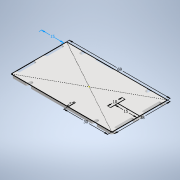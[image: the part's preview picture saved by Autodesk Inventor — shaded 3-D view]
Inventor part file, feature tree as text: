
AUTODESK INVENTOR PART (.ipt)
format: ipt  version: 2022 (Build 260153000, 153)  size: 303,616 bytes
history: native  units: mm
features: other x5, fillet x4, sketch x4, extrude x3, reference x3, projected_geometry x2, mirror x1
ambient origin geometry x8: Origin, YZ Plane, XZ Plane, XY Plane, X Axis, Y Axis, Z Axis, Center Point
bodies: Body1 (feature_tree)
feature tree (22):
  other  "Твердое тело1"
  extrude  "Выдавливание1"  Depth=69.0mm
  fillet  "Сопряжение1"  Radius=38.0mm
  fillet  "Сопряжение2"  Radius=2.0mm
  fillet  "Сопряжение3"  Radius=19.0mm
  sketch  "Эскиз2"
  extrude  "Выдавливание2"  Depth=4.0mm
  fillet  "Сопряжение4"  Radius=12.0mm
  mirror  "Зеркальное отражение1"
  extrude  "Выдавливание3"  Depth=4.0mm
  sketch  "Эскиз1"
  sketch  "Эскиз3"
  projected_geometry  "Спроецированная петля1"
  reference  "Ссылка1"
  reference  "Ссылка2"
  sketch  "Эскиз4"
  reference  "Ссылка3"
  projected_geometry  "Спроецированная петля2"
  other  "<userpath>\Documents\Git\MZCAT_battery\FastBattery.iam"
  other  "FastBattery.iam"
  other  "akkum_base1:1"
  other  "ButerBoard:1"
